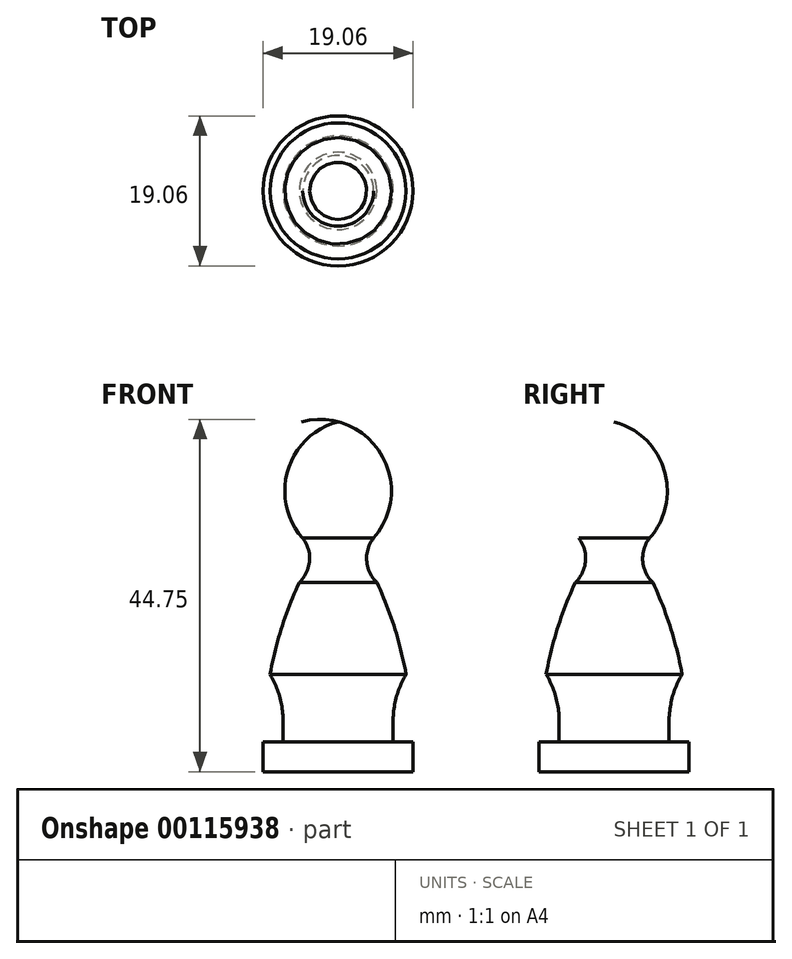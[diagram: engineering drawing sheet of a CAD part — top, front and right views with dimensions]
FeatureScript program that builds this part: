
annotation { "Feature Type Name" : "Feature", "Feature Type Description" : "" }
export const myFeature = defineFeature(function(context is Context, id is Id, definition is map)
    precondition{}
    {
        {
            var Q0;
            Q0=qCreatedBy(makeId("Front.planeOp"),FACE);
            var sketch = newSketch(context, id + "F0", { "sketchPlane" : qUnion([Q0])});
            skLineSegment(sketch, "E0", {"start": v(0, 0) * mm, "end": v(0, 44.45) * mm});
            skLineSegment(sketch, "E1", {"start": v(0, 0) * mm, "end": v(-9.53, 0) * mm});
            skLineSegment(sketch, "E2", {"start": v(-9.53, 0) * mm, "end": v(-9.53, 3.81) * mm});
            skLineSegment(sketch, "E3", {"start": v(-9.53, 3.81) * mm, "end": v(-6.99, 3.81) * mm});
            skLineSegment(sketch, "E4", {"start": v(-6.99, 3.81) * mm, "end": v(-6.99, 6.35) * mm});
            skArc(sketch, "E5", {"start": v(0, 44.45) * mm, "mid": v(-6.37, 38.31) * mm, "end": v(-4.5, 29.66) * mm});
            skArc(sketch, "E6", {"start": v(-4.92, 24.05) * mm, "mid": v(-3.63, 26.77) * mm, "end": v(-4.5, 29.66) * mm});
            skArc(sketch, "E7", {"start": v(-6.99, 6.35) * mm, "mid": v(-7.4, 9.47) * mm, "end": v(-8.63, 12.37) * mm});
            skArc(sketch, "E8", {"start": v(-4.92, 24.05) * mm, "mid": v(-7.15, 18.33) * mm, "end": v(-8.63, 12.37) * mm});
            skSolve(sketch);
        }
        {
            var Q0;
            Q0=makeQuery(id+"F0.imprint","IMPRINT",FACE,{"disambiguationData":[TD([[makeQuery(id+"F0.imprint","IMPRINT",EDGE,{"derivedFrom":sQuery(id+"F0.wireOp",EDGE,"E0")}),1.0]])]});
            var Q1;
            Q1=sQuery(id+"F0.wireOp",EDGE,"E0");
            revolve(context, id + "F1", {"entities" : qUnion([Q0]), "axis" : qUnion([Q1]), "revolveType" : RevolveType.FULL});
        }
    });
